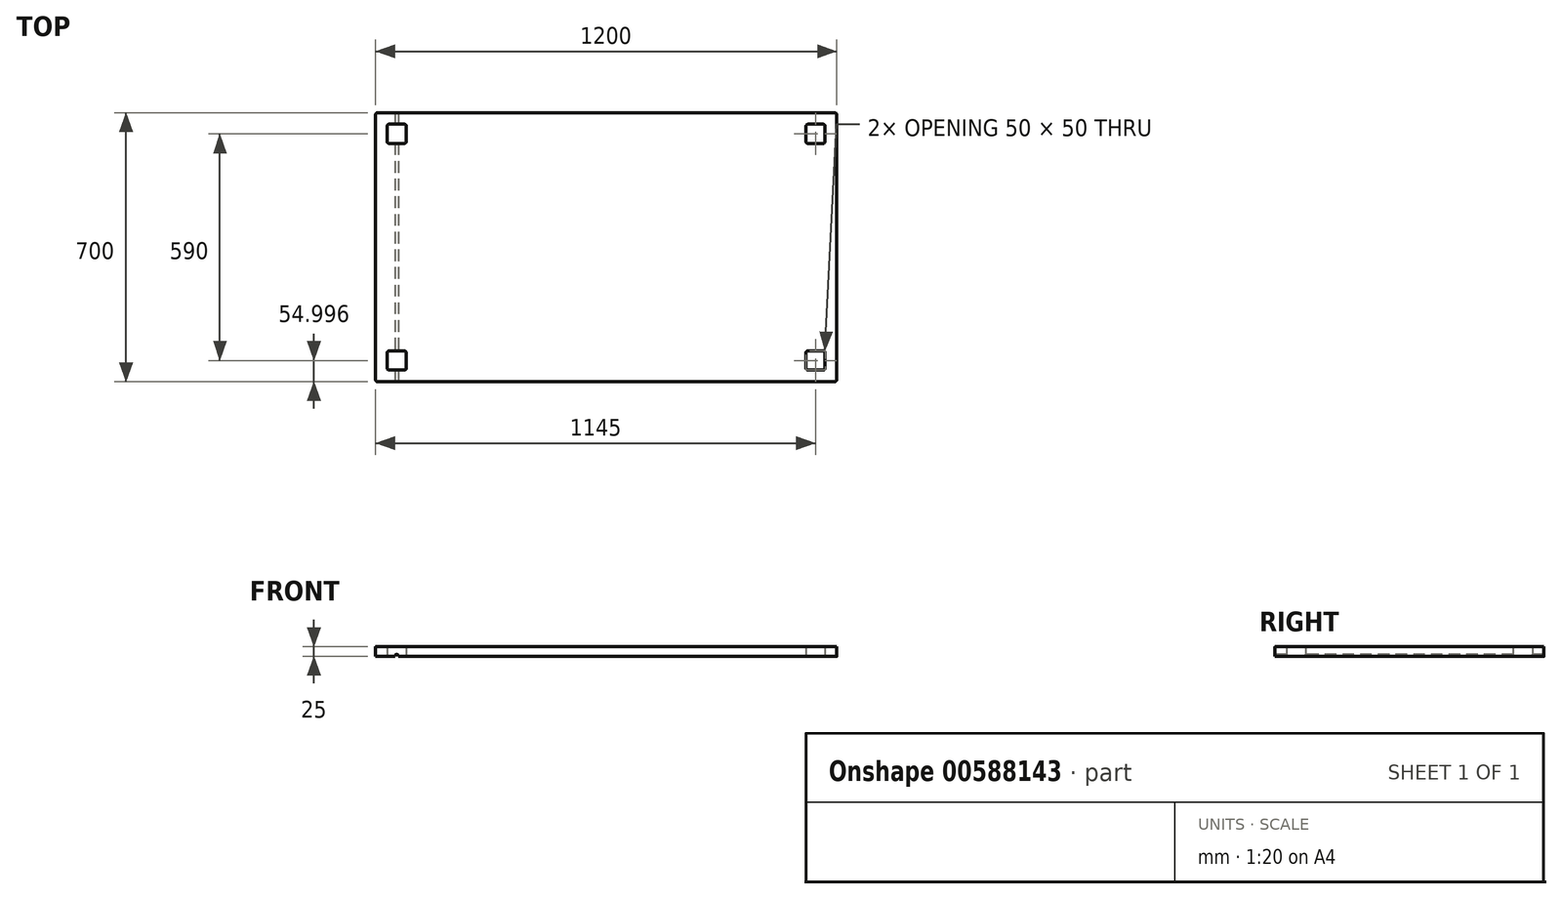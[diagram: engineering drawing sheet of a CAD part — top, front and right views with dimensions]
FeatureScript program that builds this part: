
annotation { "Feature Type Name" : "Feature", "Feature Type Description" : "" }
export const myFeature = defineFeature(function(context is Context, id is Id, definition is map)
    precondition{}
    {
        {
            var Q0;
            Q0=qCreatedBy(makeId("Top.planeOp"),FACE);
            var sketch = newSketch(context, id + "F0", { "sketchPlane" : qUnion([Q0])});
            skLineSegment(sketch, "E0.bottom", {"start": v(-626.54, 71.33) * mm, "end": v(563.46, 71.33) * mm});
            skLineSegment(sketch, "E0.top", {"start": v(-626.54, 771.33) * mm, "end": v(563.46, 771.33) * mm});
            skLineSegment(sketch, "E0.left", {"start": v(-631.54, 76.33) * mm, "end": v(-631.54, 766.33) * mm});
            skLineSegment(sketch, "E0.right", {"start": v(568.46, 76.33) * mm, "end": v(568.46, 766.33) * mm});
            skLineSegment(sketch, "E1.bottom", {"start": v(-596.54, 741.33) * mm, "end": v(-556.54, 741.33) * mm});
            skLineSegment(sketch, "E1.top", {"start": v(-596.54, 691.33) * mm, "end": v(-556.54, 691.33) * mm});
            skLineSegment(sketch, "E1.left", {"start": v(-601.54, 736.33) * mm, "end": v(-601.54, 696.33) * mm});
            skLineSegment(sketch, "E1.right", {"start": v(-551.54, 736.33) * mm, "end": v(-551.54, 696.33) * mm});
            skPoint(sketch, "E2.visualSharp", {"position": v(-601.54, 741.33) * mm});
            skArc(sketch, "E2.filletArc", {"start": v(-596.54, 741.33) * mm, "mid": v(-600.07, 739.86) * mm, "end": v(-601.54, 736.33) * mm});
            skPoint(sketch, "E3.visualSharp", {"position": v(-551.54, 741.33) * mm});
            skArc(sketch, "E3.filletArc", {"start": v(-551.54, 736.33) * mm, "mid": v(-553, 739.86) * mm, "end": v(-556.54, 741.33) * mm});
            skPoint(sketch, "E4.visualSharp", {"position": v(-551.54, 691.33) * mm});
            skArc(sketch, "E4.filletArc", {"start": v(-556.54, 691.33) * mm, "mid": v(-553, 692.8) * mm, "end": v(-551.54, 696.33) * mm});
            skPoint(sketch, "E5.visualSharp", {"position": v(-601.54, 691.33) * mm});
            skArc(sketch, "E5.filletArc", {"start": v(-601.54, 696.33) * mm, "mid": v(-600.07, 692.8) * mm, "end": v(-596.54, 691.33) * mm});
            skLineSegment(sketch, "E6.bottom", {"start": v(493.46, 741.33) * mm, "end": v(533.46, 741.33) * mm});
            skLineSegment(sketch, "E6.top", {"start": v(493.46, 691.33) * mm, "end": v(533.46, 691.33) * mm});
            skLineSegment(sketch, "E6.left", {"start": v(488.46, 736.33) * mm, "end": v(488.46, 696.33) * mm});
            skLineSegment(sketch, "E6.right", {"start": v(538.46, 736.33) * mm, "end": v(538.46, 696.33) * mm});
            skPoint(sketch, "E7.visualSharp", {"position": v(488.46, 741.33) * mm});
            skArc(sketch, "E7.filletArc", {"start": v(493.46, 741.33) * mm, "mid": v(489.93, 739.86) * mm, "end": v(488.46, 736.33) * mm});
            skPoint(sketch, "E8.visualSharp", {"position": v(538.46, 741.33) * mm});
            skArc(sketch, "E8.filletArc", {"start": v(538.46, 736.33) * mm, "mid": v(537, 739.86) * mm, "end": v(533.46, 741.33) * mm});
            skPoint(sketch, "E9.visualSharp", {"position": v(538.46, 691.33) * mm});
            skArc(sketch, "E9.filletArc", {"start": v(533.46, 691.33) * mm, "mid": v(537, 692.8) * mm, "end": v(538.46, 696.33) * mm});
            skPoint(sketch, "E10.visualSharp", {"position": v(488.46, 691.33) * mm});
            skArc(sketch, "E10.filletArc", {"start": v(488.46, 696.33) * mm, "mid": v(489.93, 692.8) * mm, "end": v(493.46, 691.33) * mm});
            skLineSegment(sketch, "E11.bottom", {"start": v(-596.54, 151.33) * mm, "end": v(-556.54, 151.33) * mm});
            skLineSegment(sketch, "E11.top", {"start": v(-596.54, 101.33) * mm, "end": v(-556.54, 101.33) * mm});
            skLineSegment(sketch, "E11.left", {"start": v(-601.54, 146.33) * mm, "end": v(-601.54, 106.33) * mm});
            skLineSegment(sketch, "E11.right", {"start": v(-551.54, 146.33) * mm, "end": v(-551.54, 106.33) * mm});
            skPoint(sketch, "E12.visualSharp", {"position": v(-601.54, 151.33) * mm});
            skArc(sketch, "E12.filletArc", {"start": v(-596.54, 151.33) * mm, "mid": v(-600.07, 149.86) * mm, "end": v(-601.54, 146.33) * mm});
            skPoint(sketch, "E13.visualSharp", {"position": v(-551.54, 151.33) * mm});
            skArc(sketch, "E13.filletArc", {"start": v(-551.54, 146.33) * mm, "mid": v(-553, 149.86) * mm, "end": v(-556.54, 151.33) * mm});
            skPoint(sketch, "E14.visualSharp", {"position": v(-551.54, 101.33) * mm});
            skArc(sketch, "E14.filletArc", {"start": v(-556.54, 101.33) * mm, "mid": v(-553, 102.8) * mm, "end": v(-551.54, 106.33) * mm});
            skPoint(sketch, "E15.visualSharp", {"position": v(-601.54, 101.33) * mm});
            skArc(sketch, "E15.filletArc", {"start": v(-601.54, 106.33) * mm, "mid": v(-600.07, 102.8) * mm, "end": v(-596.54, 101.33) * mm});
            skLineSegment(sketch, "E16.bottom", {"start": v(493.46, 151.33) * mm, "end": v(533.46, 151.33) * mm});
            skLineSegment(sketch, "E16.top", {"start": v(493.46, 101.33) * mm, "end": v(533.46, 101.33) * mm});
            skLineSegment(sketch, "E16.left", {"start": v(488.46, 146.33) * mm, "end": v(488.46, 106.33) * mm});
            skLineSegment(sketch, "E16.right", {"start": v(538.46, 146.33) * mm, "end": v(538.46, 106.33) * mm});
            skPoint(sketch, "E17.visualSharp", {"position": v(488.46, 151.33) * mm});
            skArc(sketch, "E17.filletArc", {"start": v(493.46, 151.33) * mm, "mid": v(489.93, 149.86) * mm, "end": v(488.46, 146.33) * mm});
            skPoint(sketch, "E18.visualSharp", {"position": v(538.46, 151.33) * mm});
            skArc(sketch, "E18.filletArc", {"start": v(538.46, 146.33) * mm, "mid": v(537, 149.86) * mm, "end": v(533.46, 151.33) * mm});
            skPoint(sketch, "E19.visualSharp", {"position": v(538.46, 101.33) * mm});
            skArc(sketch, "E19.filletArc", {"start": v(533.46, 101.33) * mm, "mid": v(537, 102.8) * mm, "end": v(538.46, 106.33) * mm});
            skPoint(sketch, "E20.visualSharp", {"position": v(488.46, 101.33) * mm});
            skArc(sketch, "E20.filletArc", {"start": v(488.46, 106.33) * mm, "mid": v(489.93, 102.8) * mm, "end": v(493.46, 101.33) * mm});
            skPoint(sketch, "E21.visualSharp", {"position": v(-631.54, 771.33) * mm});
            skArc(sketch, "E21.filletArc", {"start": v(-626.54, 771.33) * mm, "mid": v(-630.07, 769.86) * mm, "end": v(-631.54, 766.33) * mm});
            skPoint(sketch, "E22.visualSharp", {"position": v(568.46, 771.33) * mm});
            skArc(sketch, "E22.filletArc", {"start": v(568.46, 766.33) * mm, "mid": v(567, 769.86) * mm, "end": v(563.46, 771.33) * mm});
            skPoint(sketch, "E23.visualSharp", {"position": v(568.46, 71.33) * mm});
            skArc(sketch, "E23.filletArc", {"start": v(563.46, 71.33) * mm, "mid": v(567, 72.8) * mm, "end": v(568.46, 76.33) * mm});
            skPoint(sketch, "E24.visualSharp", {"position": v(-631.54, 71.33) * mm});
            skArc(sketch, "E24.filletArc", {"start": v(-631.54, 76.33) * mm, "mid": v(-630.07, 72.8) * mm, "end": v(-626.54, 71.33) * mm});
            skSolve(sketch);
        }
        {
            var Q0;
            Q0 = qSketchRegion(id + "F0", true);
            extrude(context, id + "F1", {"entities" : qUnion([Q0]), "endBound" : BoundingType.SYMMETRIC, "depth" : 25 * mm, "offsetDistance" : 25 * mm});
        }
        {
            var Q0;
            Q0=makeQuery(id+"F1.opExtrude","CAP_FACE",FACE,{"disambiguationData":[OSD([sQuery(id+"F0.wireOp",EDGE,"E0.bottom"),sQuery(id+"F0.wireOp",EDGE,"E0.top"),sQuery(id+"F0.wireOp",EDGE,"E0.left"),sQuery(id+"F0.wireOp",EDGE,"E0.right"),sQuery(id+"F0.wireOp",EDGE,"E1.bottom"),sQuery(id+"F0.wireOp",EDGE,"E1.top"),sQuery(id+"F0.wireOp",EDGE,"E1.left"),sQuery(id+"F0.wireOp",EDGE,"E1.right"),sQuery(id+"F0.wireOp",EDGE,"E2.filletArc"),sQuery(id+"F0.wireOp",EDGE,"E3.filletArc"),sQuery(id+"F0.wireOp",EDGE,"E4.filletArc"),sQuery(id+"F0.wireOp",EDGE,"E5.filletArc"),sQuery(id+"F0.wireOp",EDGE,"E6.bottom"),sQuery(id+"F0.wireOp",EDGE,"E6.top"),sQuery(id+"F0.wireOp",EDGE,"E6.left"),sQuery(id+"F0.wireOp",EDGE,"E6.right"),sQuery(id+"F0.wireOp",EDGE,"E7.filletArc"),sQuery(id+"F0.wireOp",EDGE,"E8.filletArc"),sQuery(id+"F0.wireOp",EDGE,"E9.filletArc"),sQuery(id+"F0.wireOp",EDGE,"E10.filletArc"),sQuery(id+"F0.wireOp",EDGE,"E11.bottom"),sQuery(id+"F0.wireOp",EDGE,"E11.top"),sQuery(id+"F0.wireOp",EDGE,"E11.left"),sQuery(id+"F0.wireOp",EDGE,"E11.right"),sQuery(id+"F0.wireOp",EDGE,"E12.filletArc"),sQuery(id+"F0.wireOp",EDGE,"E13.filletArc"),sQuery(id+"F0.wireOp",EDGE,"E14.filletArc"),sQuery(id+"F0.wireOp",EDGE,"E15.filletArc"),sQuery(id+"F0.wireOp",EDGE,"E16.bottom"),sQuery(id+"F0.wireOp",EDGE,"E16.top"),sQuery(id+"F0.wireOp",EDGE,"E16.left"),sQuery(id+"F0.wireOp",EDGE,"E16.right"),sQuery(id+"F0.wireOp",EDGE,"E17.filletArc"),sQuery(id+"F0.wireOp",EDGE,"E18.filletArc"),sQuery(id+"F0.wireOp",EDGE,"E19.filletArc"),sQuery(id+"F0.wireOp",EDGE,"E20.filletArc"),sQuery(id+"F0.wireOp",EDGE,"E21.filletArc"),sQuery(id+"F0.wireOp",EDGE,"E22.filletArc"),sQuery(id+"F0.wireOp",EDGE,"E23.filletArc"),sQuery(id+"F0.wireOp",EDGE,"E24.filletArc")])],"isStart":true});
            var sketch = newSketch(context, id + "F2", { "sketchPlane" : qUnion([Q0])});
            skLineSegment(sketch, "E25", {"start": v(-576.54, -771.33) * mm, "end": v(-576.54, -71.33) * mm});
            skPoint(sketch, "E25.startSnap0", {"position": v(-576.54, -741.33) * mm});
            skLineSegment(sketch, "E26", {"start": v(-576.54, -71.33) * mm, "end": v(-571.54, -71.33) * mm});
            skLineSegment(sketch, "E27", {"start": v(-571.54, -71.33) * mm, "end": v(-571.54, -771.33) * mm});
            skLineSegment(sketch, "E28", {"start": v(-571.54, -771.33) * mm, "end": v(-576.54, -771.33) * mm});
            skSolve(sketch);
        }
        {
            var Q0;
            {var subQ0=sQuery(id+"F2.wireOp",EDGE,"E26");Q0=makeQuery(id+"F2.imprint","IMPRINT",FACE,{"disambiguationData":[TD([[makeQuery(id+"F2.imprint","IMPRINT",EDGE,{"derivedFrom":subQ0}),-1.0]])]});}
            var Q1;
            {var subQ0=sQuery(id+"F2.wireOp",EDGE,"E25");var subQ1=makeQuery(id+"F1.opExtrude","CAP_EDGE",EDGE,{"disambiguationData":[OSD([sQuery(id+"F0.wireOp",EDGE,"E1.top")])],"isStart":true});var subQ2=makeQuery(id+"F2.imprint","INTERSECT",VERTEX,{"derivedFrom":[subQ1,subQ0]});Q1=makeQuery(id+"F2.imprint","IMPRINT",FACE,{"disambiguationData":[TD([[makeQuery(id+"F2.imprint","IMPRINT",EDGE,{"disambiguationData":[TD([[subQ2,-1.0]])],"derivedFrom":subQ0}),-1.0]])]});}
            var Q2;
            {var subQ0=sQuery(id+"F2.wireOp",EDGE,"E28");Q2=makeQuery(id+"F2.imprint","IMPRINT",FACE,{"disambiguationData":[TD([[makeQuery(id+"F2.imprint","IMPRINT",EDGE,{"derivedFrom":subQ0}),1.0]])]});}
            var Q3;
            Q3=sQuery(id+"F2.wireOp",EDGE,"E25");
            revolve(context, id + "F3", {"operationType" : NewBodyOperationType.REMOVE, "entities" : qUnion([Q0, Q1, Q2]), "axis" : qUnion([Q3]), "revolveType" : RevolveType.FULL, "oppositeDirection" : true});
        }
    });
